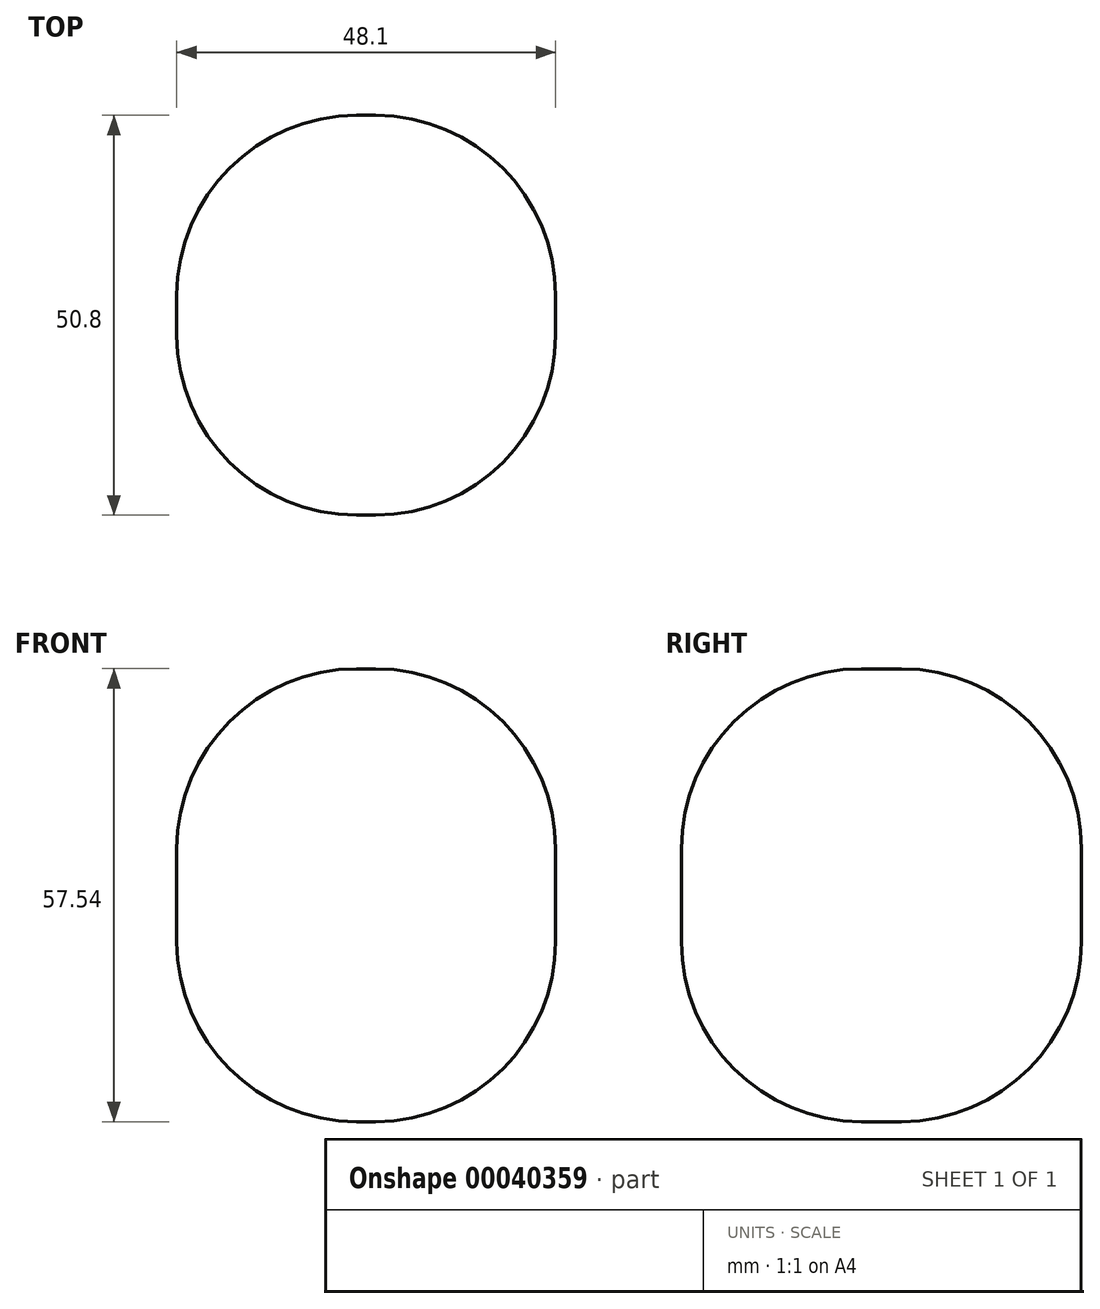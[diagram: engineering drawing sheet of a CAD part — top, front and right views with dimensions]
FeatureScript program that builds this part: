
annotation { "Feature Type Name" : "Feature", "Feature Type Description" : "" }
export const myFeature = defineFeature(function(context is Context, id is Id, definition is map)
    precondition{}
    {
        {
            var Q0;
            Q0=qCreatedBy(makeId("Front.planeOp"),FACE);
            var sketch = newSketch(context, id + "F0", { "sketchPlane" : qUnion([Q0])});
            skLineSegment(sketch, "E0", {"start": v(24.05, 0) * mm, "end": v(24.05, 28.77) * mm});
            skLineSegment(sketch, "E1", {"start": v(24.05, 28.77) * mm, "end": v(0, 28.77) * mm});
            skLineSegment(sketch, "E2.MirrorCS", {"start": v(24.05, 0) * mm, "end": v(24.05, -28.77) * mm});
            skLineSegment(sketch, "E3.MirrorCS", {"start": v(24.05, -28.77) * mm, "end": v(0, -28.77) * mm});
            skLineSegment(sketch, "E4.MirrorCS", {"start": v(-24.05, 0) * mm, "end": v(-24.05, -28.77) * mm});
            skLineSegment(sketch, "E5.MirrorCS", {"start": v(-24.05, 0) * mm, "end": v(-24.05, 28.77) * mm});
            skLineSegment(sketch, "E6.MirrorCS", {"start": v(-24.05, -28.77) * mm, "end": v(0, -28.77) * mm});
            skLineSegment(sketch, "E7.MirrorCS", {"start": v(-24.05, 28.77) * mm, "end": v(0, 28.77) * mm});
            skSolve(sketch);
        }
        {
            var Q0;
            Q0 = qSketchRegion(id + "F0", true);
            extrude(context, id + "F1", {"entities" : qUnion([Q0]), "depth" : 25.4 * mm, "hasSecondDirection" : true, "secondDirectionOppositeDirection" : true, "secondDirectionDepth" : 25.4 * mm});
        }
        {
            var Q0;
            Q0=makeQuery(id+"F1.opExtrude","CAP_FACE",FACE,{"disambiguationData":[OSD([sQuery(id+"F0.wireOp",EDGE,"E2.MirrorCS"),sQuery(id+"F0.wireOp",EDGE,"E0"),sQuery(id+"F0.wireOp",EDGE,"E1"),sQuery(id+"F0.wireOp",EDGE,"E3.MirrorCS"),sQuery(id+"F0.wireOp",EDGE,"E5.MirrorCS"),sQuery(id+"F0.wireOp",EDGE,"E4.MirrorCS"),sQuery(id+"F0.wireOp",EDGE,"E6.MirrorCS"),sQuery(id+"F0.wireOp",EDGE,"E7.MirrorCS")])],"isStart":false});
            var Q1;
            Q1=makeQuery(id+"F1.opExtrude","SWEPT_FACE",FACE,{"disambiguationData":[OSD([sQuery(id+"F0.wireOp",EDGE,"E1"),sQuery(id+"F0.wireOp",EDGE,"E7.MirrorCS")])]});
            var Q2;
            Q2=makeQuery(id+"F1.opExtrude","SWEPT_FACE",FACE,{"disambiguationData":[OSD([sQuery(id+"F0.wireOp",EDGE,"E5.MirrorCS"),sQuery(id+"F0.wireOp",EDGE,"E4.MirrorCS")])]});
            var Q3;
            Q3=makeQuery(id+"F1.opExtrude","SWEPT_FACE",FACE,{"disambiguationData":[OSD([sQuery(id+"F0.wireOp",EDGE,"E2.MirrorCS"),sQuery(id+"F0.wireOp",EDGE,"E0")])]});
            var Q4;
            Q4=makeQuery(id+"F1.opExtrude","CAP_FACE",FACE,{"disambiguationData":[OSD([sQuery(id+"F0.wireOp",EDGE,"E2.MirrorCS"),sQuery(id+"F0.wireOp",EDGE,"E0"),sQuery(id+"F0.wireOp",EDGE,"E1"),sQuery(id+"F0.wireOp",EDGE,"E3.MirrorCS"),sQuery(id+"F0.wireOp",EDGE,"E5.MirrorCS"),sQuery(id+"F0.wireOp",EDGE,"E4.MirrorCS"),sQuery(id+"F0.wireOp",EDGE,"E6.MirrorCS"),sQuery(id+"F0.wireOp",EDGE,"E7.MirrorCS")])],"isStart":true});
            fillet(context, id + "F2", {"entities" : qUnion([Q0, Q1, Q2, Q3, Q4]), "radius" : 22.86 * mm, "tangentPropagation" : true, "allowEdgeOverflow" : false});
        }
    });
